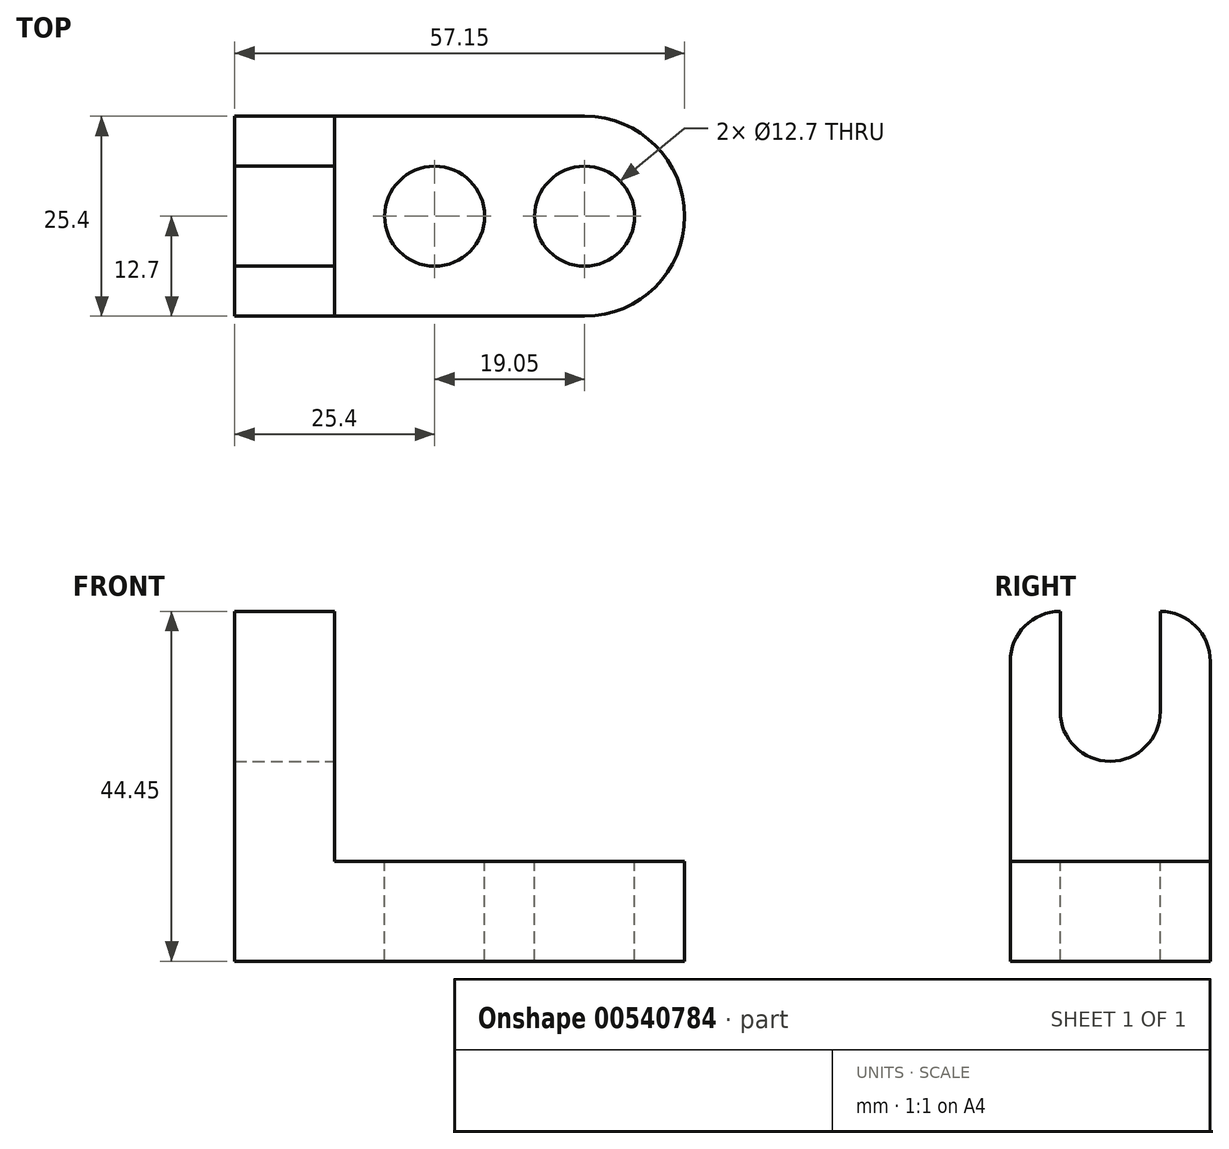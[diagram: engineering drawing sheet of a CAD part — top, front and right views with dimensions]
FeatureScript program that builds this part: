
annotation { "Feature Type Name" : "Feature", "Feature Type Description" : "" }
export const myFeature = defineFeature(function(context is Context, id is Id, definition is map)
    precondition{}
    {
        {
            var Q0;
            Q0=qCreatedBy(makeId("Front.planeOp"),FACE);
            var sketch = newSketch(context, id + "F0", { "sketchPlane" : qUnion([Q0])});
            skLineSegment(sketch, "E0", {"start": v(0, 0) * mm, "end": v(57.15, 0) * mm});
            skLineSegment(sketch, "E1", {"start": v(57.15, 0) * mm, "end": v(57.15, 12.7) * mm});
            skLineSegment(sketch, "E2", {"start": v(57.15, 12.7) * mm, "end": v(12.7, 12.7) * mm});
            skLineSegment(sketch, "E3", {"start": v(12.7, 12.7) * mm, "end": v(12.7, 44.45) * mm});
            skLineSegment(sketch, "E4", {"start": v(12.7, 44.45) * mm, "end": v(0, 44.45) * mm});
            skLineSegment(sketch, "E5", {"start": v(0, 44.45) * mm, "end": v(0, 0) * mm});
            skSolve(sketch);
        }
        {
            var Q0;
            Q0=makeQuery(id+"F0.imprint","IMPRINT",FACE,{"disambiguationData":[TD([[makeQuery(id+"F0.imprint","IMPRINT",EDGE,{"derivedFrom":sQuery(id+"F0.wireOp",EDGE,"E0")}),1.0]])]});
            extrude(context, id + "F1", {"entities" : qUnion([Q0]), "depth" : 25.4 * mm, "offsetDistance" : 25.4 * mm});
        }
        {
            var Q0;
            Q0=makeQuery(id+"F1.opExtrude","SWEPT_FACE",FACE,{"disambiguationData":[OSD([sQuery(id+"F0.wireOp",EDGE,"E3")])]});
            var sketch = newSketch(context, id + "F2", { "sketchPlane" : qUnion([Q0])});
            skCircle(sketch, "E6", {"center": v(-12.7, 31.75) * mm, "radius": 6.35 * mm});
            skPoint(sketch, "E6.perimeterSnap0", {"position": v(0, 28.57) * mm});
            skPoint(sketch, "E6.perimeterSnap1", {"position": v(-12.7, 12.7) * mm});
            skLineSegment(sketch, "E7", {"start": v(-19.05, 31.75) * mm, "end": v(-19.05, 44.45) * mm});
            skLineSegment(sketch, "E8", {"start": v(-6.35, 31.75) * mm, "end": v(-6.35, 44.45) * mm});
            skArc(sketch, "E9", {"start": v(-19.05, 44.45) * mm, "mid": v(-23.54, 42.6) * mm, "end": v(-25.4, 38.1) * mm});
            skArc(sketch, "E10", {"start": v(0, 38.1) * mm, "mid": v(-1.86, 42.6) * mm, "end": v(-6.35, 44.45) * mm});
            skSolve(sketch);
        }
        {
            var Q0;
            {var subQ0=sQuery(id+"F2.wireOp",EDGE,"E7");Q0=makeQuery(id+"F2.imprint","IMPRINT",FACE,{"disambiguationData":[TD([[makeQuery(id+"F2.imprint","IMPRINT",EDGE,{"derivedFrom":subQ0}),-1.0]])]});}
            var Q1;
            {var subQ0=sQuery(id+"F2.wireOp",EDGE,"E6");var subQ1=makeQuery(id+"F2.imprint","INTERSECT",VERTEX,{"derivedFrom":[subQ0,sQuery(id+"F2.wireOp",EDGE,"E7")]});Q1=makeQuery(id+"F2.imprint","IMPRINT",FACE,{"disambiguationData":[TD([[makeQuery(id+"F2.imprint","IMPRINT",EDGE,{"disambiguationData":[TD([[subQ1,1.0]])],"derivedFrom":subQ0}),1.0]])]});}
            var Q2;
            {var subQ0=sQuery(id+"F2.wireOp",EDGE,"E10");Q2=makeQuery(id+"F2.imprint","IMPRINT",FACE,{"disambiguationData":[TD([[makeQuery(id+"F2.imprint","IMPRINT",EDGE,{"derivedFrom":subQ0}),-1.0]])]});}
            var Q3;
            {var subQ0=sQuery(id+"F2.wireOp",EDGE,"E9");Q3=makeQuery(id+"F2.imprint","IMPRINT",FACE,{"disambiguationData":[TD([[makeQuery(id+"F2.imprint","IMPRINT",EDGE,{"derivedFrom":subQ0}),-1.0]])]});}
            extrude(context, id + "F3", {"entities" : qUnion([Q0, Q1, Q2, Q3]), "operationType" : NewBodyOperationType.REMOVE, "oppositeDirection" : true, "depth" : 12.7 * mm, "offsetDistance" : 25.4 * mm});
        }
        {
            var Q0;
            Q0=makeQuery(id+"F1.opExtrude","SWEPT_FACE",FACE,{"disambiguationData":[OSD([sQuery(id+"F0.wireOp",EDGE,"E2")])]});
            var sketch = newSketch(context, id + "F4", { "sketchPlane" : qUnion([Q0])});
            skCircle(sketch, "E11", {"center": v(25.4, -12.7) * mm, "radius": 6.35 * mm});
            skCircle(sketch, "E12", {"center": v(44.45, -12.7) * mm, "radius": 6.35 * mm});
            skArc(sketch, "E13", {"start": v(44.45, -25.4) * mm, "mid": v(57.15, -12.7) * mm, "end": v(44.45, 0) * mm});
            skSolve(sketch);
        }
        {
            var Q0;
            Q0=makeQuery(id+"F4.imprint","IMPRINT",FACE,{"disambiguationData":[TD([[makeQuery(id+"F4.imprint","IMPRINT",EDGE,{"derivedFrom":sQuery(id+"F4.wireOp",EDGE,"E11")}),1.0]])]});
            var Q1;
            Q1=makeQuery(id+"F4.imprint","IMPRINT",FACE,{"disambiguationData":[TD([[makeQuery(id+"F4.imprint","IMPRINT",EDGE,{"derivedFrom":sQuery(id+"F4.wireOp",EDGE,"E12")}),1.0]])]});
            var Q2;
            {var subQ0=sQuery(id+"F4.wireOp",EDGE,"E13");var subQ1=sQuery(id+"F0.wireOp",EDGE,"E2");var subQ2=makeQuery(id+"F1.opExtrude","CAP_EDGE",EDGE,{"disambiguationData":[OSD([subQ1])],"isStart":false});var subQ3=makeQuery(id+"F4.imprint","INTERSECT",VERTEX,{"derivedFrom":[subQ2,subQ0]});Q2=makeQuery(id+"F4.imprint","IMPRINT",FACE,{"disambiguationData":[TD([[makeQuery(id+"F4.imprint","IMPRINT",EDGE,{"disambiguationData":[TD([[subQ3,-1.0]])],"derivedFrom":subQ0}),-1.0]])]});}
            var Q3;
            {var subQ0=sQuery(id+"F4.wireOp",EDGE,"E13");var subQ1=sQuery(id+"F0.wireOp",EDGE,"E2");var subQ2=makeQuery(id+"F1.opExtrude","CAP_EDGE",EDGE,{"disambiguationData":[OSD([subQ1])],"isStart":true});var subQ3=makeQuery(id+"F4.imprint","INTERSECT",VERTEX,{"derivedFrom":[subQ2,subQ0]});Q3=makeQuery(id+"F4.imprint","IMPRINT",FACE,{"disambiguationData":[TD([[makeQuery(id+"F4.imprint","IMPRINT",EDGE,{"disambiguationData":[TD([[subQ3,1.0]])],"derivedFrom":subQ0}),-1.0]])]});}
            extrude(context, id + "F5", {"entities" : qUnion([Q0, Q1, Q2, Q3]), "operationType" : NewBodyOperationType.REMOVE, "oppositeDirection" : true, "depth" : 12.7 * mm, "offsetDistance" : 25.4 * mm});
        }
    });
